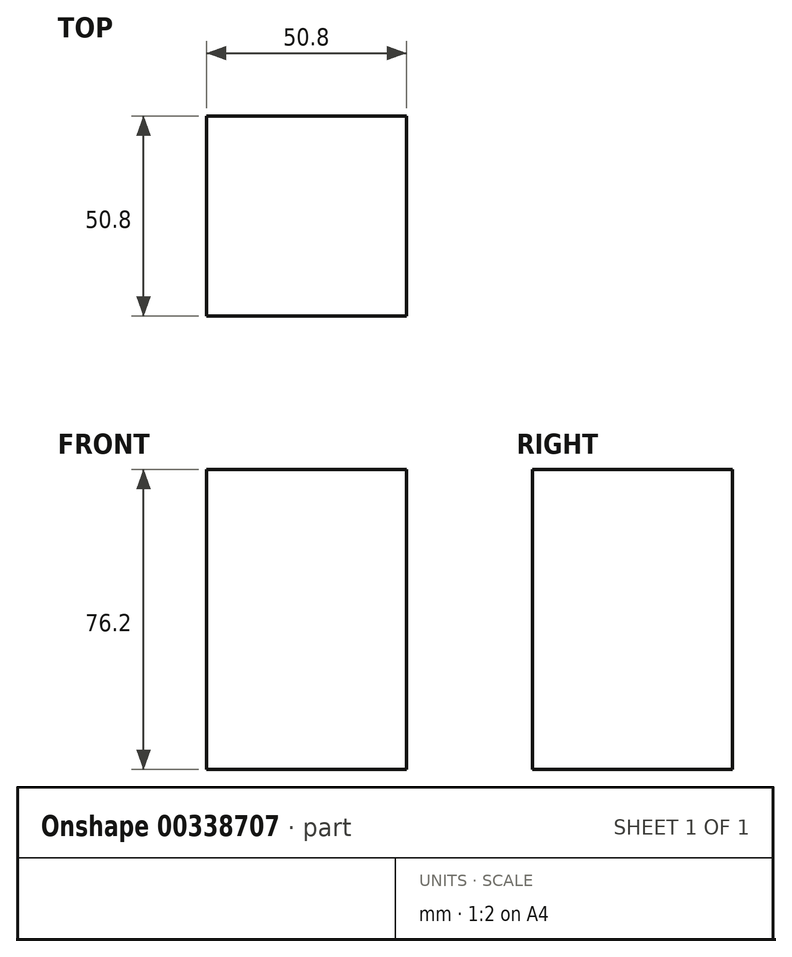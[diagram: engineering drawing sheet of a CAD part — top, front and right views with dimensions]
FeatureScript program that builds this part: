
annotation { "Feature Type Name" : "Feature", "Feature Type Description" : "" }
export const myFeature = defineFeature(function(context is Context, id is Id, definition is map)
    precondition{}
    {
        {
            var Q0;
            Q0=qCreatedBy(makeId("Top.planeOp"),FACE);
            var sketch = newSketch(context, id + "F0", { "sketchPlane" : qUnion([Q0])});
            skLineSegment(sketch, "E0.bottom", {"start": v(-50.28, 57.3) * mm, "end": v(51.32, 57.3) * mm});
            skLineSegment(sketch, "E0.top", {"start": v(-50.28, -44.3) * mm, "end": v(51.32, -44.3) * mm});
            skLineSegment(sketch, "E0.left", {"start": v(-50.28, 57.3) * mm, "end": v(-50.28, -44.3) * mm});
            skLineSegment(sketch, "E0.right", {"start": v(51.32, 57.3) * mm, "end": v(51.32, -44.3) * mm});
            skSolve(sketch);
        }
        {
            var Q0;
            Q0=makeQuery(id+"F0.imprint","IMPRINT",FACE,{"disambiguationData":[TD([[makeQuery(id+"F0.imprint","IMPRINT",EDGE,{"derivedFrom":sQuery(id+"F0.wireOp",EDGE,"E0.bottom")}),-1.0]])]});
            extrude(context, id + "F1", {"entities" : qUnion([Q0]), "depth" : 152.4 * mm});
        }
        {
            var Q0;
            Q0=makeQuery(id+"F1.opExtrude","SWEPT_BODY",BODY,{"disambiguationData":[OSD([sQuery(id+"F0.wireOp",EDGE,"E0.bottom"),sQuery(id+"F0.wireOp",EDGE,"E0.top"),sQuery(id+"F0.wireOp",EDGE,"E0.left"),sQuery(id+"F0.wireOp",EDGE,"E0.right")])]});
            deleteBodies(context, id + "F2", {"entities" : qUnion([Q0])});
        }
        {
            var Q0;
            Q0=qCreatedBy(makeId("Top.planeOp"),FACE);
            var sketch = newSketch(context, id + "F3", { "sketchPlane" : qUnion([Q0])});
            skLineSegment(sketch, "E1.bottom", {"start": v(-30.61, 23.96) * mm, "end": v(20.19, 23.96) * mm});
            skLineSegment(sketch, "E1.top", {"start": v(-30.61, -26.84) * mm, "end": v(20.19, -26.84) * mm});
            skLineSegment(sketch, "E1.left", {"start": v(-30.61, 23.96) * mm, "end": v(-30.61, -26.84) * mm});
            skLineSegment(sketch, "E1.right", {"start": v(20.19, 23.96) * mm, "end": v(20.19, -26.84) * mm});
            skSolve(sketch);
        }
        {
            var Q0;
            Q0=makeQuery(id+"F3.imprint","IMPRINT",FACE,{"disambiguationData":[TD([[makeQuery(id+"F3.imprint","IMPRINT",EDGE,{"derivedFrom":sQuery(id+"F3.wireOp",EDGE,"E1.bottom")}),-1.0]])]});
            extrude(context, id + "F4", {"entities" : qUnion([Q0]), "depth" : 76.2 * mm});
        }
    });
